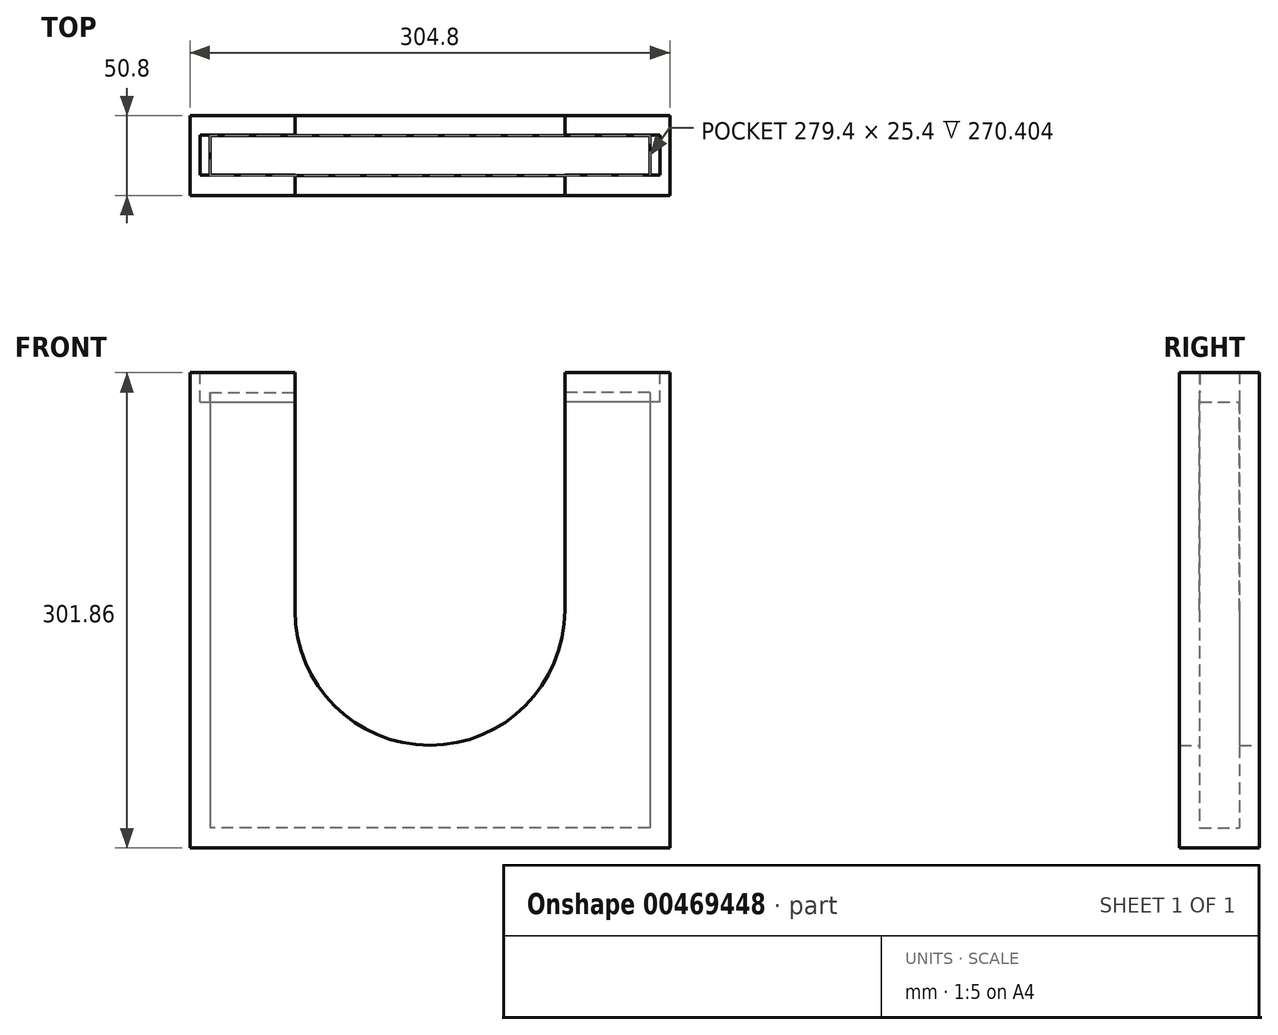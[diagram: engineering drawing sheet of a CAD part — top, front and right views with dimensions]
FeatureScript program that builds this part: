
annotation { "Feature Type Name" : "Feature", "Feature Type Description" : "" }
export const myFeature = defineFeature(function(context is Context, id is Id, definition is map)
    precondition{}
    {
        {
            var Q0;
            Q0=qCreatedBy(makeId("Front.planeOp"),FACE);
            var sketch = newSketch(context, id + "F0", { "sketchPlane" : qUnion([Q0])});
            skLineSegment(sketch, "E0.bottom", {"start": v(152.4, 150.93) * mm, "end": v(-152.4, 150.93) * mm});
            skLineSegment(sketch, "E0.top", {"start": v(152.4, -150.93) * mm, "end": v(-152.4, -150.93) * mm});
            skLineSegment(sketch, "E0.left", {"start": v(152.4, 150.93) * mm, "end": v(152.4, -150.93) * mm});
            skLineSegment(sketch, "E0.right", {"start": v(-152.4, 150.93) * mm, "end": v(-152.4, -150.93) * mm});
            skPoint(sketch, "E0.middle", {"position": v(0, 0) * mm});
            skCircle(sketch, "E1", {"center": v(0, 0) * mm, "radius": 85.73 * mm});
            skLineSegment(sketch, "E2.bottom", {"start": v(85.72, 0) * mm, "end": v(-85.73, 0) * mm});
            skLineSegment(sketch, "E2.top", {"start": v(85.72, 150.93) * mm, "end": v(-85.73, 150.93) * mm});
            skLineSegment(sketch, "E2.left", {"start": v(85.73, 0) * mm, "end": v(85.73, 150.93) * mm});
            skLineSegment(sketch, "E2.right", {"start": v(-85.73, 0) * mm, "end": v(-85.73, 150.93) * mm});
            skSolve(sketch);
        }
        {
            var Q0;
            Q0=makeQuery(id+"F0.imprint","IMPRINT",FACE,{"disambiguationData":[TD([[makeQuery(id+"F0.imprint","IMPRINT",EDGE,{"derivedFrom":sQuery(id+"F0.wireOp",EDGE,"E0.bottom")}),1.0]])]});
            extrude(context, id + "F1", {"entities" : qUnion([Q0]), "depth" : 50.8 * mm});
        }
        {
            var Q0;
            Q0=makeQuery(id+"F1.opExtrude","SWEPT_FACE",FACE,{"disambiguationData":[OSD([sQuery(id+"F0.wireOp",EDGE,"E2.left")])]});
            var Q1;
            Q1=makeQuery(id+"F1.opExtrude","SWEPT_FACE",FACE,{"disambiguationData":[OSD([sQuery(id+"F0.wireOp",EDGE,"E1")])]});
            var Q2;
            Q2=makeQuery(id+"F1.opExtrude","SWEPT_FACE",FACE,{"disambiguationData":[OSD([sQuery(id+"F0.wireOp",EDGE,"E2.right")])]});
            shell(context, id + "F2", {"entities" : qUnion([Q0, Q1, Q2]), "thickness" : 12.7 * mm});
        }
        {
            var Q0;
            Q0=qCreatedBy(makeId("Right.planeOp"),FACE);
            var sketch = newSketch(context, id + "F3", { "sketchPlane" : qUnion([Q0])});
            skLineSegment(sketch, "E3.bottom", {"start": v(-37.85, 132.17) * mm, "end": v(-12.45, 132.17) * mm});
            skLineSegment(sketch, "E3.top", {"start": v(-37.85, 170.27) * mm, "end": v(-12.45, 170.27) * mm});
            skLineSegment(sketch, "E3.left", {"start": v(-37.85, 132.17) * mm, "end": v(-37.85, 170.27) * mm});
            skLineSegment(sketch, "E3.right", {"start": v(-12.45, 132.17) * mm, "end": v(-12.45, 170.27) * mm});
            skPoint(sketch, "E3.middle", {"position": v(-25.15, 151.22) * mm});
            skSolve(sketch);
        }
        {
            var Q0;
            Q0=makeQuery(id+"F3.imprint","IMPRINT",FACE,{"disambiguationData":[TD([[makeQuery(id+"F3.imprint","IMPRINT",EDGE,{"derivedFrom":sQuery(id+"F3.wireOp",EDGE,"E3.bottom")}),1.0]])]});
            extrude(context, id + "F4", {"entities" : qUnion([Q0]), "operationType" : NewBodyOperationType.REMOVE, "oppositeDirection" : true, "depth" : 146.05 * mm});
        }
        {
            var Q0;
            Q0 = qSketchRegion(id + "F3", true);
            extrude(context, id + "F5", {"entities" : qUnion([Q0]), "operationType" : NewBodyOperationType.REMOVE, "depth" : 146.05 * mm});
        }
    });
